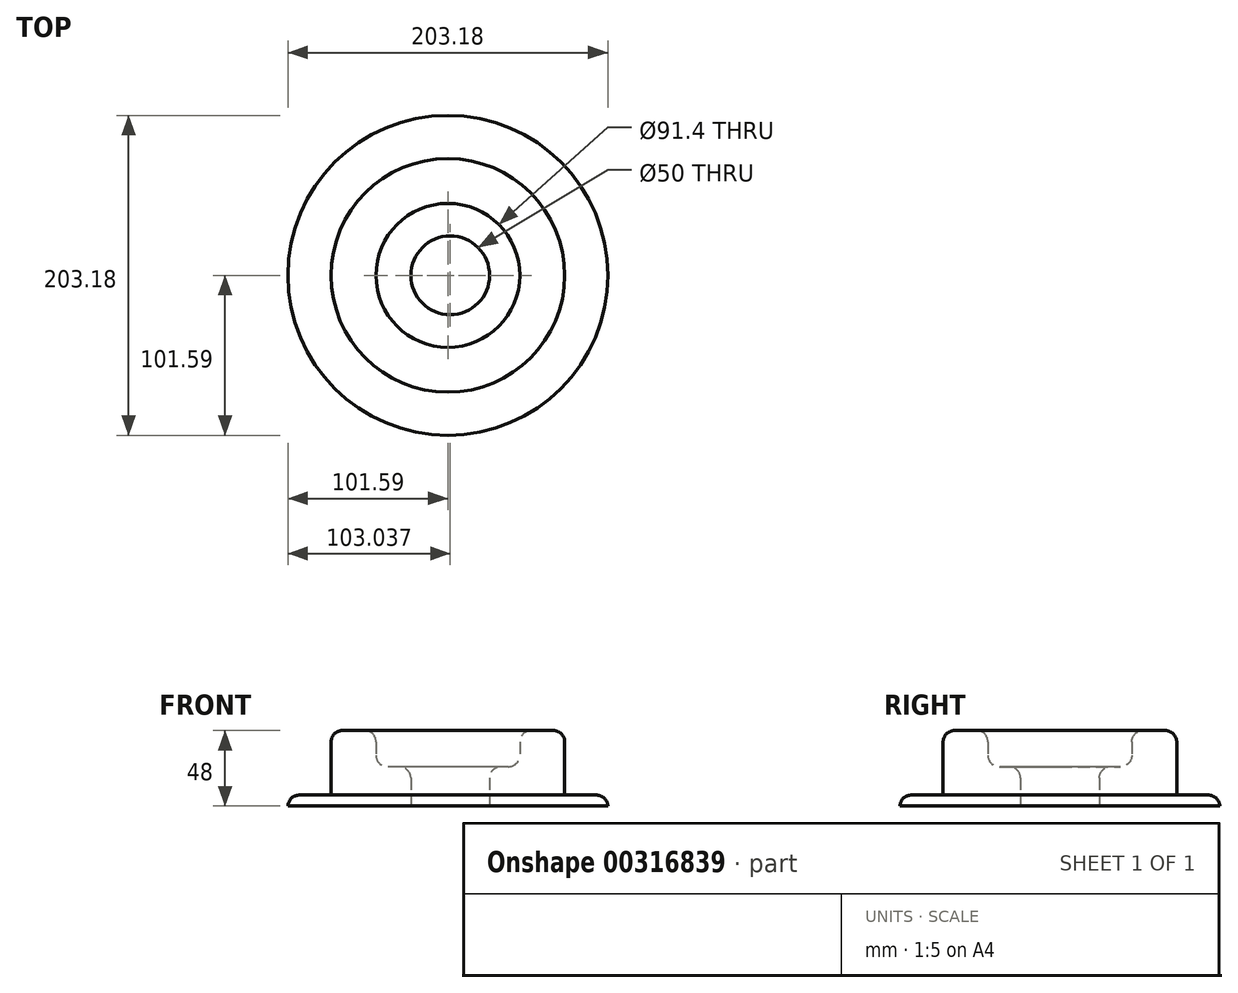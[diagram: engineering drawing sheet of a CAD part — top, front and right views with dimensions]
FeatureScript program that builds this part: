
annotation { "Feature Type Name" : "Feature", "Feature Type Description" : "" }
export const myFeature = defineFeature(function(context is Context, id is Id, definition is map)
    precondition{}
    {
        {
            var Q0;
            Q0=qCreatedBy(makeId("Top.planeOp"),FACE);
            var sketch = newSketch(context, id + "F0", { "sketchPlane" : qUnion([Q0])});
            skCircle(sketch, "E0", {"center": v(1.45, 0) * mm, "radius": 25 * mm});
            skCircle(sketch, "E1", {"center": v(1.45, 0) * mm, "radius": 50 * mm});
            skSolve(sketch);
        }
        {
            var Q0;
            Q0=qCreatedBy(makeId("Top.planeOp"),FACE);
            var sketch = newSketch(context, id + "F1", { "sketchPlane" : qUnion([Q0])});
            skCircle(sketch, "E2", {"center": v(0, 0) * mm, "radius": 101.6 * mm});
            skCircle(sketch, "E3", {"center": v(0, 0) * mm, "radius": 74.17 * mm});
            skCircle(sketch, "E4", {"center": v(0, 0) * mm, "radius": 45.7 * mm});
            skSolve(sketch);
        }
        {
            var Q0;
            Q0=makeQuery(id+"F1.imprint","IMPRINT",FACE,{"disambiguationData":[TD([[makeQuery(id+"F1.imprint","IMPRINT",EDGE,{"derivedFrom":sQuery(id+"F1.wireOp",EDGE,"E3")}),1.0]])]});
            extrude(context, id + "F2", {"entities" : qUnion([Q0]), "depth" : 48 * mm});
        }
        {
            var Q0;
            Q0=makeQuery(id+"F0.imprint","IMPRINT",FACE,{"disambiguationData":[TD([[makeQuery(id+"F0.imprint","IMPRINT",EDGE,{"derivedFrom":sQuery(id+"F0.wireOp",EDGE,"E0")}),-1.0]])]});
            extrude(context, id + "F3", {"entities" : qUnion([Q0]), "operationType" : NewBodyOperationType.ADD, "depth" : 25 * mm});
        }
        {
            var Q0;
            Q0=makeQuery(id+"FRNbBGACGfy8ymq_1.opExtrude","CAP_FACE",FACE,{"disambiguationData":[OSD([sQuery(id+"F1.wireOp",EDGE,"E2"),sQuery(id+"F1.wireOp",EDGE,"E3")])],"isStart":false});
            var Q1;
            {var subQ0=sQuery(id+"F0.wireOp",EDGE,"E1");Q1=makeQuery(id+"F3.boolean.opBoolean","SPLIT",FACE,{"disambiguationData":[TD([makeQuery(id+"F2.opExtrude","SWEPT_FACE",FACE,{"disambiguationData":[OSD([sQuery(id+"F1.wireOp",EDGE,"E3")])]})])],"derivedFrom":makeQuery(id+"F3.opExtrude","CAP_FACE",FACE,{"disambiguationData":[OSD([sQuery(id+"F0.wireOp",EDGE,"E0"),subQ0])],"isStart":false})});}
            var Q2;
            Q2=makeQuery(id+"F2.opExtrude","CAP_FACE",FACE,{"disambiguationData":[OSD([sQuery(id+"F1.wireOp",EDGE,"E3"),sQuery(id+"F1.wireOp",EDGE,"E4")])],"isStart":false});
            fillet(context, id + "F4", {"entities" : qUnion([Q0, Q1, Q2]), "radius" : 7.24 * mm, "tangentPropagation" : true, "allowEdgeOverflow" : false});
        }
        {
            var Q0;
            Q0=makeQuery(id+"F1.imprint","IMPRINT",FACE,{"disambiguationData":[TD([[makeQuery(id+"F1.imprint","IMPRINT",EDGE,{"derivedFrom":sQuery(id+"F1.wireOp",EDGE,"E2")}),1.0]])]});
            extrude(context, id + "F5", {"entities" : qUnion([Q0]), "operationType" : NewBodyOperationType.ADD, "depth" : 7 * mm});
        }
        {
            var Q0;
            Q0=makeQuery(id+"F5.opExtrude","CAP_EDGE",EDGE,{"disambiguationData":[OSD([sQuery(id+"F1.wireOp",EDGE,"E2")])],"isStart":false});
            var Q1;
            Q1=makeQuery(id+"F5.opExtrude","CAP_EDGE",EDGE,{"disambiguationData":[OSD([sQuery(id+"F1.wireOp",EDGE,"E3")])],"isStart":false});
            fillet(context, id + "F6", {"entities" : qUnion([Q0, Q1]), "radius" : 7.24 * mm, "tangentPropagation" : true, "allowEdgeOverflow" : false});
        }
    });
